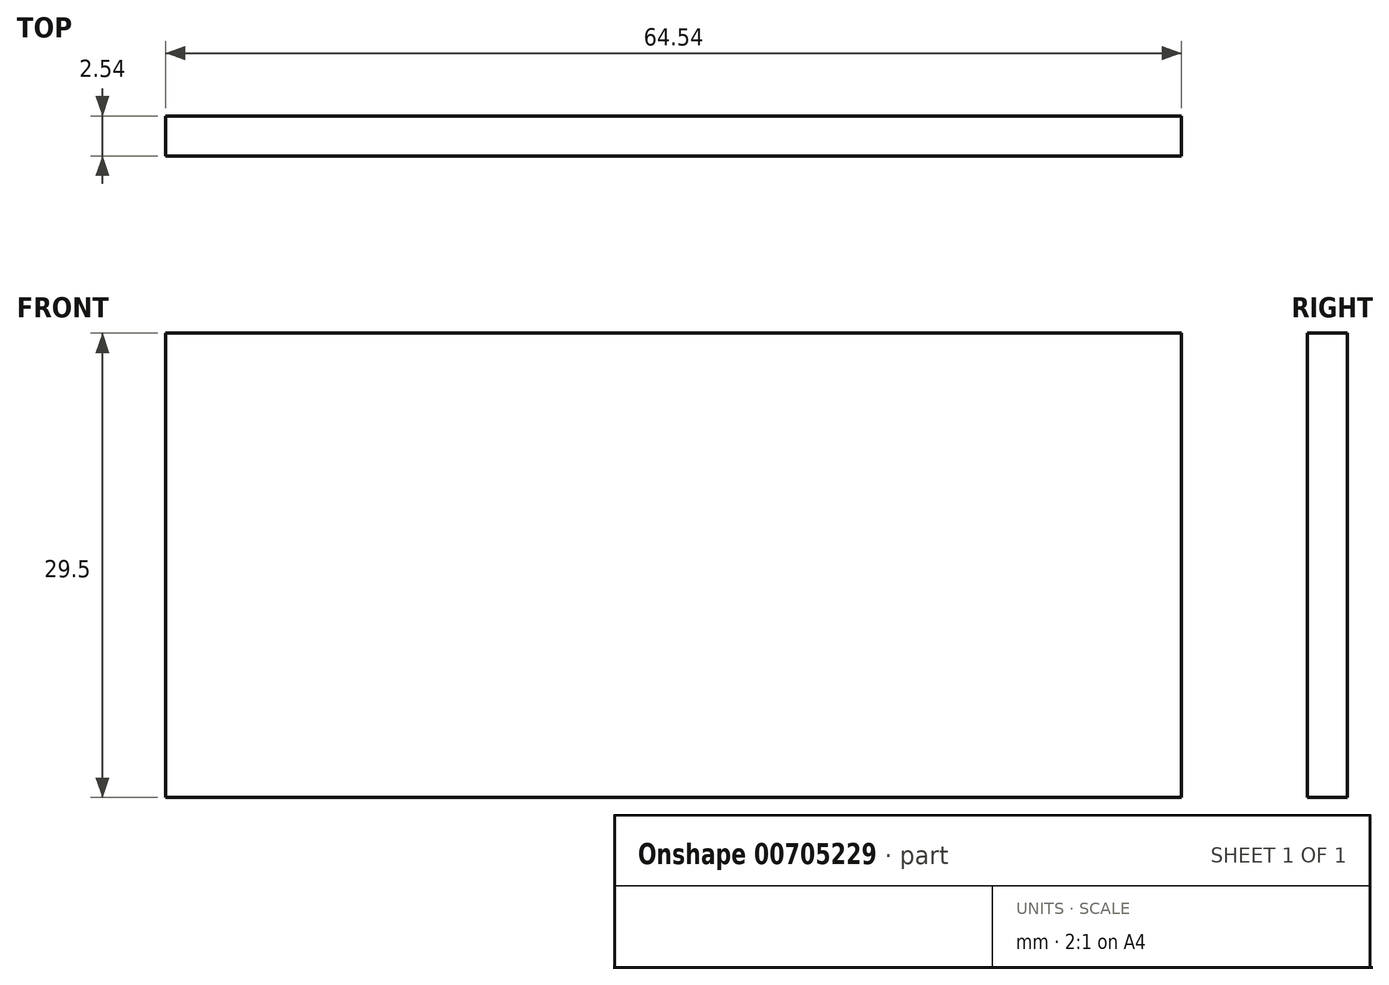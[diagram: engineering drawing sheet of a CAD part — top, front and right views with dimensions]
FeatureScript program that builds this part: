
annotation { "Feature Type Name" : "Feature", "Feature Type Description" : "" }
export const myFeature = defineFeature(function(context is Context, id is Id, definition is map)
    precondition{}
    {
        {
            var Q0;
            Q0=qCreatedBy(makeId("Front.planeOp"),FACE);
            var sketch = newSketch(context, id + "F0", { "sketchPlane" : qUnion([Q0])});
            skLineSegment(sketch, "E0.bottom", {"start": v(32.27, 14.75) * mm, "end": v(-32.27, 14.75) * mm});
            skLineSegment(sketch, "E0.top", {"start": v(32.27, -14.75) * mm, "end": v(-32.27, -14.75) * mm});
            skLineSegment(sketch, "E0.left", {"start": v(32.27, 14.75) * mm, "end": v(32.27, -14.75) * mm});
            skLineSegment(sketch, "E0.right", {"start": v(-32.27, 14.75) * mm, "end": v(-32.27, -14.75) * mm});
            skPoint(sketch, "E0.middle", {"position": v(0, 0) * mm});
            skSolve(sketch);
        }
        {
            var Q0;
            Q0 = qSketchRegion(id + "F0", true);
            extrude(context, id + "F1", {"entities" : qUnion([Q0]), "depth" : 2.54 * mm, "offsetDistance" : 25.4 * mm});
        }
    });
